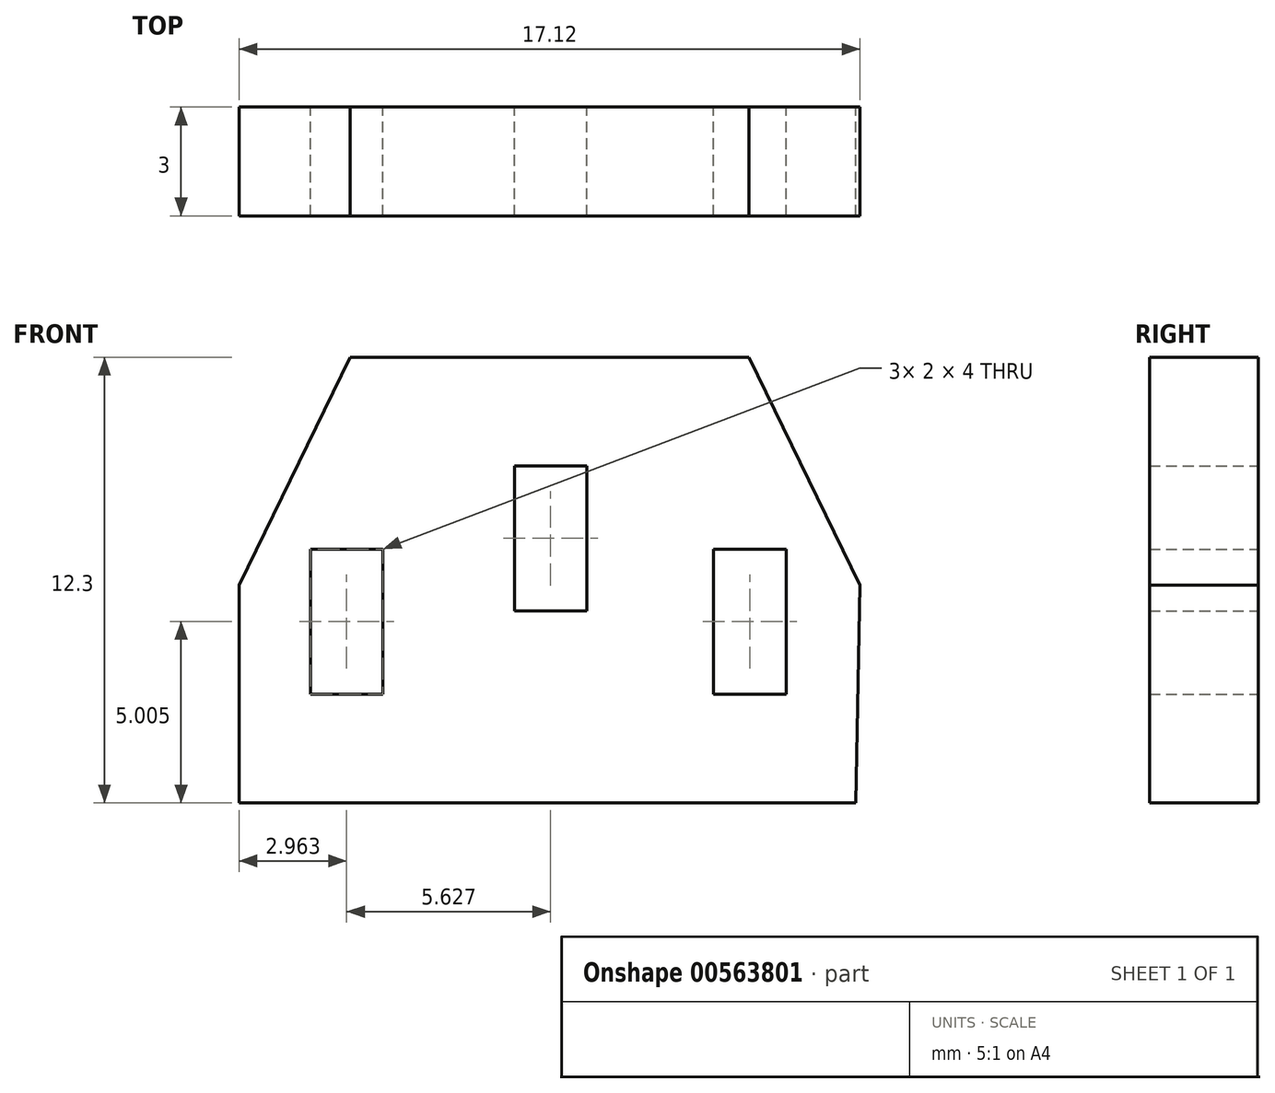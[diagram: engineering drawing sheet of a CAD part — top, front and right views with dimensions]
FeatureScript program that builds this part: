
annotation { "Feature Type Name" : "Feature", "Feature Type Description" : "" }
export const myFeature = defineFeature(function(context is Context, id is Id, definition is map)
    precondition{}
    {
        {
            var Q0;
            Q0=qCreatedBy(makeId("Front.planeOp"),FACE);
            var sketch = newSketch(context, id + "F0", { "sketchPlane" : qUnion([Q0])});
            skLineSegment(sketch, "E0", {"start": v(-6.53, 15.72) * mm, "end": v(4.47, 15.72) * mm});
            skLineSegment(sketch, "E1", {"start": v(4.47, 15.72) * mm, "end": v(7.53, 9.42) * mm});
            skLineSegment(sketch, "E2", {"start": v(-6.53, 15.72) * mm, "end": v(-9.59, 9.42) * mm});
            skLineSegment(sketch, "E3", {"start": v(-9.59, 9.42) * mm, "end": v(-9.59, 3.42) * mm});
            skLineSegment(sketch, "E4", {"start": v(-9.59, 3.42) * mm, "end": v(7.41, 3.42) * mm});
            skLineSegment(sketch, "E5", {"start": v(7.41, 3.42) * mm, "end": v(7.53, 9.42) * mm});
            skSolve(sketch);
        }
        {
            var Q0;
            Q0=qCreatedBy(makeId("Front.planeOp"),FACE);
            var sketch = newSketch(context, id + "F1", { "sketchPlane" : qUnion([Q0])});
            skLineSegment(sketch, "E6.bottom", {"start": v(0, 12.72) * mm, "end": v(-2, 12.72) * mm});
            skLineSegment(sketch, "E6.top", {"start": v(0, 8.72) * mm, "end": v(-2, 8.72) * mm});
            skLineSegment(sketch, "E6.left", {"start": v(0, 12.72) * mm, "end": v(0, 8.72) * mm});
            skLineSegment(sketch, "E6.right", {"start": v(-2, 12.72) * mm, "end": v(-2, 8.72) * mm});
            skLineSegment(sketch, "E7.bottom", {"start": v(5.5, 10.42) * mm, "end": v(3.5, 10.42) * mm});
            skLineSegment(sketch, "E7.left", {"start": v(5.5, 10.42) * mm, "end": v(5.5, 6.42) * mm});
            skLineSegment(sketch, "E7.right", {"start": v(3.5, 10.42) * mm, "end": v(3.5, 6.42) * mm});
            skLineSegment(sketch, "E8.bottom", {"start": v(-5.63, 10.42) * mm, "end": v(-7.63, 10.42) * mm});
            skLineSegment(sketch, "E8.left", {"start": v(-5.63, 10.42) * mm, "end": v(-5.63, 6.42) * mm});
            skLineSegment(sketch, "E9", {"start": v(3.5, 6.42) * mm, "end": v(5.5, 6.42) * mm});
            skLineSegment(sketch, "E10", {"start": v(-5.63, 6.42) * mm, "end": v(-7.63, 6.42) * mm});
            skLineSegment(sketch, "E11", {"start": v(-7.63, 6.42) * mm, "end": v(-7.63, 10.42) * mm});
            skSolve(sketch);
        }
        {
            var Q0;
            Q0=makeQuery(id+"F0.imprint","IMPRINT",FACE,{"disambiguationData":[TD([[makeQuery(id+"F0.imprint","IMPRINT",EDGE,{"derivedFrom":sQuery(id+"F0.wireOp",EDGE,"E0")}),-1.0]])]});
            extrude(context, id + "F2", {"entities" : qUnion([Q0]), "depth" : 3 * mm, "offsetDistance" : 25 * mm});
        }
        {
            var Q0;
            Q0=makeQuery(id+"F1.imprint","IMPRINT",FACE,{"disambiguationData":[TD([[makeQuery(id+"F1.imprint","IMPRINT",EDGE,{"derivedFrom":sQuery(id+"F1.wireOp",EDGE,"E7.bottom")}),1.0]])]});
            var Q1;
            Q1=makeQuery(id+"F1.imprint","IMPRINT",FACE,{"disambiguationData":[TD([[makeQuery(id+"F1.imprint","IMPRINT",EDGE,{"derivedFrom":sQuery(id+"F1.wireOp",EDGE,"E6.bottom")}),1.0]])]});
            var Q2;
            Q2=makeQuery(id+"F1.imprint","IMPRINT",FACE,{"disambiguationData":[TD([[makeQuery(id+"F1.imprint","IMPRINT",EDGE,{"derivedFrom":sQuery(id+"F1.wireOp",EDGE,"E8.bottom")}),1.0]])]});
            extrude(context, id + "F3", {"entities" : qUnion([Q0, Q1, Q2]), "operationType" : NewBodyOperationType.REMOVE, "depth" : 3 * mm, "offsetDistance" : 25 * mm});
        }
    });
